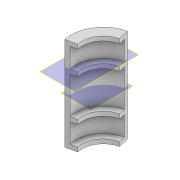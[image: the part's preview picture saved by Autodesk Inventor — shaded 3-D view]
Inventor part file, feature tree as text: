
AUTODESK INVENTOR PART (.ipt)
format: ipt  version: 2021 (Build 250183000, 183)  size: 156,672 bytes
history: native  units: in
note: dims shown in document units (in); Inventor stores cm internally (conversion verified against a paired STEP export)
features: plane x4, sketch x4, extrude x3, mirror x2, emboss x1, split x1, projected_geometry x1, other x1, surface_op x1
ambient origin geometry x8: Origin, YZ Plane, XZ Plane, XY Plane, X Axis, Y Axis, Z Axis, Center Point
bodies: Solid2 (feature_tree), Solid3 (feature_tree)
feature tree (18):
  extrude  "Extrusion1"  Depth=0.0394in
  extrude  "Extrusion2"  TaperAngle=90.0deg  [1 undecoded]
  mirror  "Mirror1"
  plane  "Work Plane2"
  extrude  "Extrusion3"  Depth=0.0394in
  mirror  "Mirror2"
  plane  "Work Plane4"
  emboss  "Emboss1"
  split  "Split1"
  sketch  "Sketch1"  dims[d0=0.2953in d1=0.0394in]
  sketch  "Sketch2"  dims[d2=0.7804in d3=0.0in d4=90.0deg]
  plane  "Work Plane1"
  sketch  "Sketch3"  dims[d6=0.0394in d7=0.0in d9=0.0984in]
  projected_geometry  "Projected Loop1"
  plane  "Work Plane3"
  sketch  "Sketch4"  dims[d10=0.1811in d11=0.0394in d12=0.0in d13=0.375in d14=0.0197in d15=0.0in d16=0.1969in d17=0.1969in d18=0.1969in d19=0.1969in d20=0.0in]
  other  "Srf1"
  surface_op  "Boundary Patch1"
note: 1 required parameter value undecoded (feature->parameter linkage not recoverable at this tier; creation-order binding heuristic only, values carry confidence <= 0.55)
